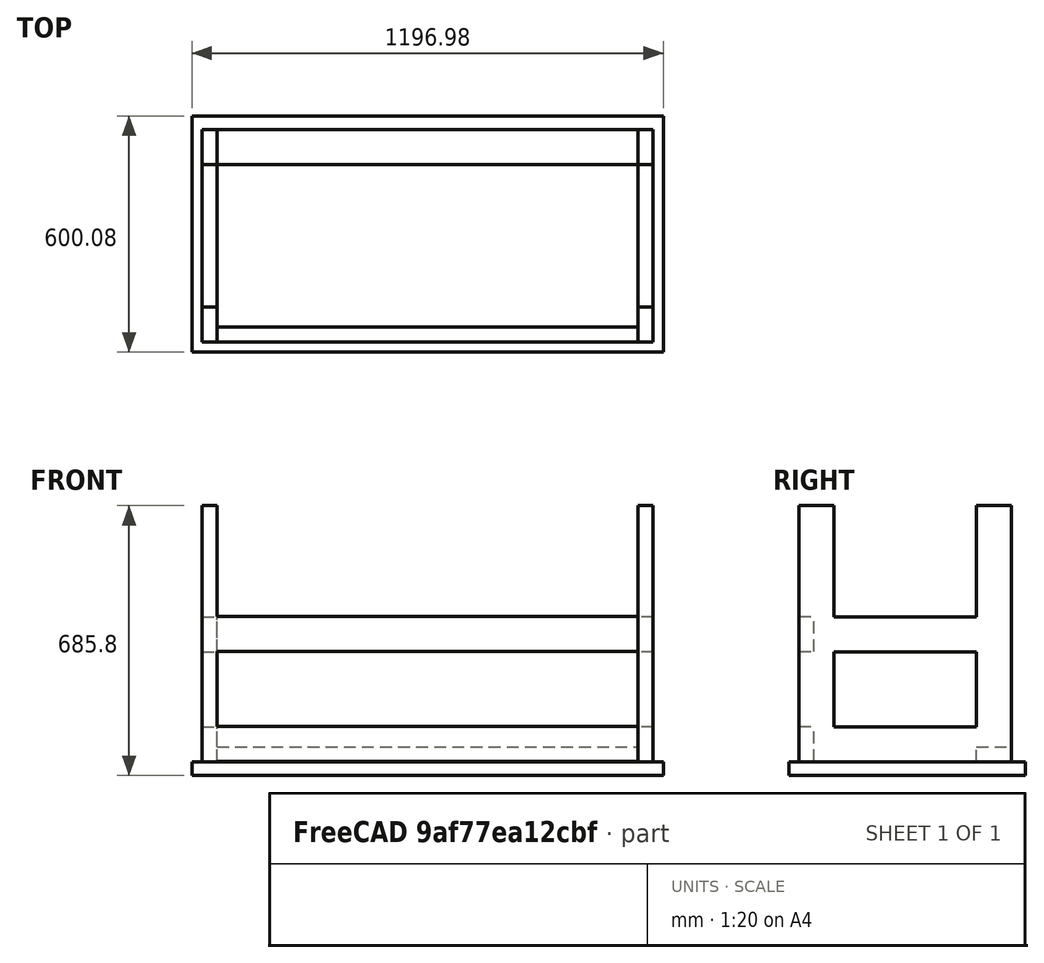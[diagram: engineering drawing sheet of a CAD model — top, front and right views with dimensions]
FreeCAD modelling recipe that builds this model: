
FCSTD DOCUMENT  (FreeCAD 0.18R16146 (Git))
Label: desk
License: All rights reserved
LicenseURL: http://en.wikipedia.org/wiki/All_rights_reserved
objects: TechDraw::DrawViewDimension×14, Part::Box×7, Part::Mirroring×5, App::MeasureDistance×4, TechDraw::DrawViewPart×4, Part::Compound×2, TechDraw::DrawSVGTemplate×1, Part::FeaturePython×1, TechDraw::DrawPage×1
note: 15 computed .brp shape members not serialized (recipe doc carries the construction recipe); baked Part::Feature solids carry a one-line shape summary decoded from their .brp

FEATURE [Part::Box] Box  label="tabletop"
  AttacherType = Attacher::AttachEngine3D
  Height = 34.925
  Length = 1196.98
  Width = 600.075
FEATURE [App::MeasureDistance] Distance  label="Distance: 1+3/8""
  Distance = 34.925
  P1 = (57.2676,600.075,0)
  P2 = (57.2676,600.075,34.925)
FEATURE [App::MeasureDistance] Distance001  label="Distance: 1' 11+1/4""
  Distance = 591.435
  P1 = (7.99408,591.406,34.925)
  P2 = (13.8558,0,34.925)
FEATURE [App::MeasureDistance] Distance002  label="Distance: 3' 11+1/8""
  Distance = 1197
  P1 = (0,0,18.8969)
  P2 = (1196.98,0,11.1818)
FEATURE [Part::Box] Box001  label="leg_br"
  AttacherType = Attacher::AttachEngine3D
  Height = 650.875
  Length = 38.1
  Placement = pos=(25.4,25.4,34.925) rot=(0,0,1;0rad)
  Width = 88.9
FEATURE [Part::Mirroring] Part__Mirroring  label="leg_br (Mirror #1)"
  Base = (0,295.275,0)
  Normal = (0,1,0)
  Source = -> Box001
FEATURE [Part::Mirroring] Part__Mirroring001  label="leg_br (Mirror #2)"
  Base = (598.487,0,0)
  Normal = (1,0,0)
  Source = -> Box001
FEATURE [Part::Mirroring] Part__Mirroring002  label="leg_br (Mirror #3)"
  Base = (598.487,0,0)
  Normal = (1,0,0)
  Source = -> Part__Mirroring
FEATURE [Part::Box] Box002  label="back_support"
  AttacherType = Attacher::AttachEngine3D
  Height = 88.9
  Length = 1069.97
  Placement = pos=(63.5,25.4,214) rot=(0,0,1;0rad)
  Width = 38.1
FEATURE [Part::Box] Box003  label="side_support"
  AttacherType = Attacher::AttachEngine3D
  Height = 88.9
  Length = 38.1
  Placement = pos=(25.4,114.3,212.725) rot=(0,0,1;0rad)
  Width = 361.95
FEATURE [App::MeasureDistance] Distance003  label="Distance: 1' 2+1/4""
  Distance = 361.959
  P1 = (25.4,476.25,683.291)
  P2 = (25.4,114.3,685.8)
FEATURE [Part::Mirroring] Part__Mirroring003  label="side_support (Mirror #4)"
  Base = (598.487,0,0)
  Normal = (1,0,0)
  Source = -> Box003
FEATURE [Part::Compound] Compound  label="Braces_lower"
  Links = -> [Part__Mirroring003,Box002,Box003]
  Placement = pos=(0,0,101.6) rot=(0,0,1;0rad)
FEATURE [Part::Box] Box004  label="back_support001"
  AttacherType = Attacher::AttachEngine3D
  Height = 88.9
  Length = 1069.97
  Placement = pos=(63.5,25.4,214) rot=(0,0,1;0rad)
  Width = 38.1
FEATURE [Part::Box] Box005  label="side_support001"
  AttacherType = Attacher::AttachEngine3D
  Height = 88.9
  Length = 38.1
  Placement = pos=(25.4,114.3,212.725) rot=(0,0,1;0rad)
  Width = 361.95
FEATURE [Part::Mirroring] Part__Mirroring004  label="side_support (Mirror #4)001"
  Base = (598.487,0,0)
  Normal = (1,0,0)
  Source = -> Box005
FEATURE [Part::Compound] Compound001  label="Braces_upper"
  Links = -> [Part__Mirroring004,Box004,Box005]
  Placement = pos=(0,0,-178) rot=(0,0,1;0rad)
FEATURE [Part::Box] Box006  label="Brace_front"
  AttacherType = Attacher::AttachEngine3D
  Height = 38.1
  Length = 1069.97
  Placement = pos=(63.5,476.25,34.925) rot=(0,0,1;0rad)
  Width = 88.9
FEATURE [TechDraw::DrawSVGTemplate] Template
  EditableTexts = Designed_by_Name=Sean Fischer; Drawing_number=1; FC-Date=1/12/2020; FC-SC=-; FC-SH=1/1; FC-Title=Custom Desk; Weight=-
  Height = 210
  Orientation = 1
  Width = 297
FEATURE [Part::FeaturePython] Connect  label="Frame"  # WARN: FeaturePython — macro-defined, semantics opaque (R4)
  Objects = -> [Part__Mirroring002,Part__Mirroring001,Compound,Compound001,Box006,Box001,Part__Mirroring]
  Tolerance = 0
FEATURE [TechDraw::DrawViewPart] View  label="ISO"
  CoarseView = false
  Direction = (-0.577,0.577,0.577)
  Focus = 98.425
  HardHidden = false
  IsoCount = 0
  IsoHidden = false
  IsoVisible = false
  LockPosition = false
  Perspective = false
  Rotation = 0
  Scale = 0.07
  ScaleType = 2
  SeamHidden = false
  SeamVisible = false
  SmoothHidden = false
  SmoothVisible = false
  Source = -> [Connect]
  X = 80
  Y = 134.192
FEATURE [TechDraw::DrawViewPart] View001  label="SIDE"
  CoarseView = false
  Direction = (-1,0,0)
  Focus = 100
  HardHidden = false
  IsoCount = 0
  IsoHidden = false
  IsoVisible = false
  LockPosition = false
  Perspective = false
  Rotation = 0
  Scale = 0.07
  ScaleType = 2
  SeamHidden = false
  SeamVisible = false
  SmoothHidden = false
  SmoothVisible = false
  Source = -> [Connect]
  X = 255.41
  Y = 130
FEATURE [TechDraw::DrawViewPart] View002  label="FRONT"
  CoarseView = false
  Direction = (0,1,0)
  Focus = 100
  HardHidden = false
  IsoCount = 0
  IsoHidden = false
  IsoVisible = false
  LockPosition = false
  Perspective = false
  Rotation = 0
  Scale = 0.07
  ScaleType = 0
  SeamHidden = false
  SeamVisible = false
  SmoothHidden = false
  SmoothVisible = false
  Source = -> [Connect]
  X = 80
  Y = 47.5619
FEATURE [TechDraw::DrawViewPart] View003  label="REAR"
  CoarseView = false
  Direction = (0,-1,0)
  Focus = 100
  HardHidden = false
  IsoCount = 0
  IsoHidden = false
  IsoVisible = false
  LockPosition = false
  Perspective = false
  Rotation = 0
  Scale = 0.07
  ScaleType = 0
  SeamHidden = false
  SeamVisible = false
  SmoothHidden = false
  SmoothVisible = false
  Source = -> [Connect]
  X = 176.789
  Y = 130
FEATURE [TechDraw::DrawViewDimension] Dimension
  Arbitrary = false
  FormatSpec = %.2f
  LockPosition = false
  MeasureType = 1
  OverTolerance = 0
  References2D = -> [View003]
  Rotation = 0
  ScaleType = 0
  Type = 1
  UnderTolerance = 0
  X = 0
  Y = -35
FEATURE [TechDraw::DrawViewDimension] Dimension002
  Arbitrary = false
  FormatSpec = %.2f
  LockPosition = false
  MeasureType = 1
  OverTolerance = 0
  References2D = -> [View001]
  Rotation = 0
  ScaleType = 0
  Type = 1
  UnderTolerance = 0
  X = -0.25
  Y = -35
FEATURE [TechDraw::DrawViewDimension] Dimension003
  Arbitrary = false
  FormatSpec = %.2f
  LockPosition = false
  MeasureType = 1
  OverTolerance = 0
  References2D = -> [View001]
  Rotation = 0
  ScaleType = 0
  Type = 0
  UnderTolerance = 0
  X = 1.39741
  Y = 35
FEATURE [TechDraw::DrawViewDimension] Dimension004
  Arbitrary = false
  FormatSpec = %.2f
  LockPosition = false
  MeasureType = 1
  OverTolerance = 0
  References2D = -> [View002]
  Rotation = 0
  ScaleType = 0
  Type = 2
  UnderTolerance = 0
  X = -55.02
  Y = -0.458804
FEATURE [TechDraw::DrawViewDimension] Dimension005
  Arbitrary = false
  FormatSpec = %.2f
  LockPosition = false
  MeasureType = 1
  OverTolerance = 0
  References2D = -> [View002]
  Rotation = 0
  ScaleType = 0
  Type = 2
  UnderTolerance = 0
  X = 45
  Y = -10.4996
FEATURE [TechDraw::DrawViewDimension] Dimension006
  Arbitrary = false
  FormatSpec = %.2f
  LockPosition = false
  MeasureType = 1
  OverTolerance = 0
  References2D = -> [View002]
  Rotation = 0
  ScaleType = 0
  Type = 2
  UnderTolerance = 0
  X = 45
  Y = 11.7776
FEATURE [TechDraw::DrawViewDimension] Dimension007
  Arbitrary = false
  FormatSpec = %.2f
  LockPosition = false
  MeasureType = 1
  OverTolerance = 0
  References2D = -> [View003]
  Rotation = 0
  ScaleType = 0
  Type = 1
  UnderTolerance = 0
  X = -0.698846
  Y = 45.7177
FEATURE [TechDraw::DrawViewDimension] Dimension008
  Arbitrary = false
  FormatSpec = %.2f
  LockPosition = false
  MeasureType = 1
  OverTolerance = 0
  References2D = -> [View001]
  Rotation = 0
  ScaleType = 0
  Type = 1
  UnderTolerance = 0
  X = -4.12866
  Y = 12.7323
FEATURE [TechDraw::DrawViewDimension] Dimension009
  Arbitrary = false
  FormatSpec = %.2f
  LockPosition = false
  MeasureType = 1
  OverTolerance = 0
  References2D = -> [View002]
  Rotation = 0
  ScaleType = 0
  Type = 1
  UnderTolerance = 0
  X = -26.8765
  Y = 17.0472
FEATURE [TechDraw::DrawViewDimension] Dimension010
  Arbitrary = false
  FormatSpec = %.2f
  LockPosition = false
  MeasureType = 1
  OverTolerance = 0
  References2D = -> [View003]
  Rotation = 0
  ScaleType = 0
  Type = 1
  UnderTolerance = 0
  X = -23.4747
  Y = 15.7715
FEATURE [TechDraw::DrawViewDimension] Dimension011
  Arbitrary = false
  FormatSpec = %.2f
  LockPosition = false
  MeasureType = 1
  OverTolerance = 0
  References2D = -> [View003]
  Rotation = 0
  ScaleType = 0
  Type = 2
  UnderTolerance = 0
  X = 45
  Y = -9.58827
FEATURE [TechDraw::DrawViewDimension] Dimension012
  Arbitrary = false
  FormatSpec = %.2f
  LockPosition = false
  MeasureType = 1
  OverTolerance = 0
  References2D = -> [View003]
  Rotation = 0
  ScaleType = 0
  Type = 2
  UnderTolerance = 0
  X = 45
  Y = 13.3673
FEATURE [TechDraw::DrawViewDimension] Dimension013
  Arbitrary = false
  FormatSpec = %.2f
  LockPosition = false
  MeasureType = 1
  OverTolerance = 0
  References2D = -> [View003]
  Rotation = 0
  ScaleType = 0
  Type = 2
  UnderTolerance = 0
  X = -14.6999
  Y = 11.0408
FEATURE [TechDraw::DrawViewDimension] Dimension014
  Arbitrary = false
  FormatSpec = %.2f
  LockPosition = false
  MeasureType = 1
  OverTolerance = 0
  References2D = -> [View002]
  Rotation = 0
  ScaleType = 0
  Type = 2
  UnderTolerance = 0
  X = -19.5303
  Y = 11.2534
FEATURE [TechDraw::DrawPage] Page  label="Drawing"
  KeepUpdated = true
  ProjectionType = 0
  Template = -> Template
  Views = -> [View,View001,View002,View003,Dimension,Dimension002,Dimension003,Dimension004,Dimension005,Dimension006,Dimension007,Dimension008,Dimension009,Dimension010,Dimension011,Dimension012,Dimension013,Dimension014]
